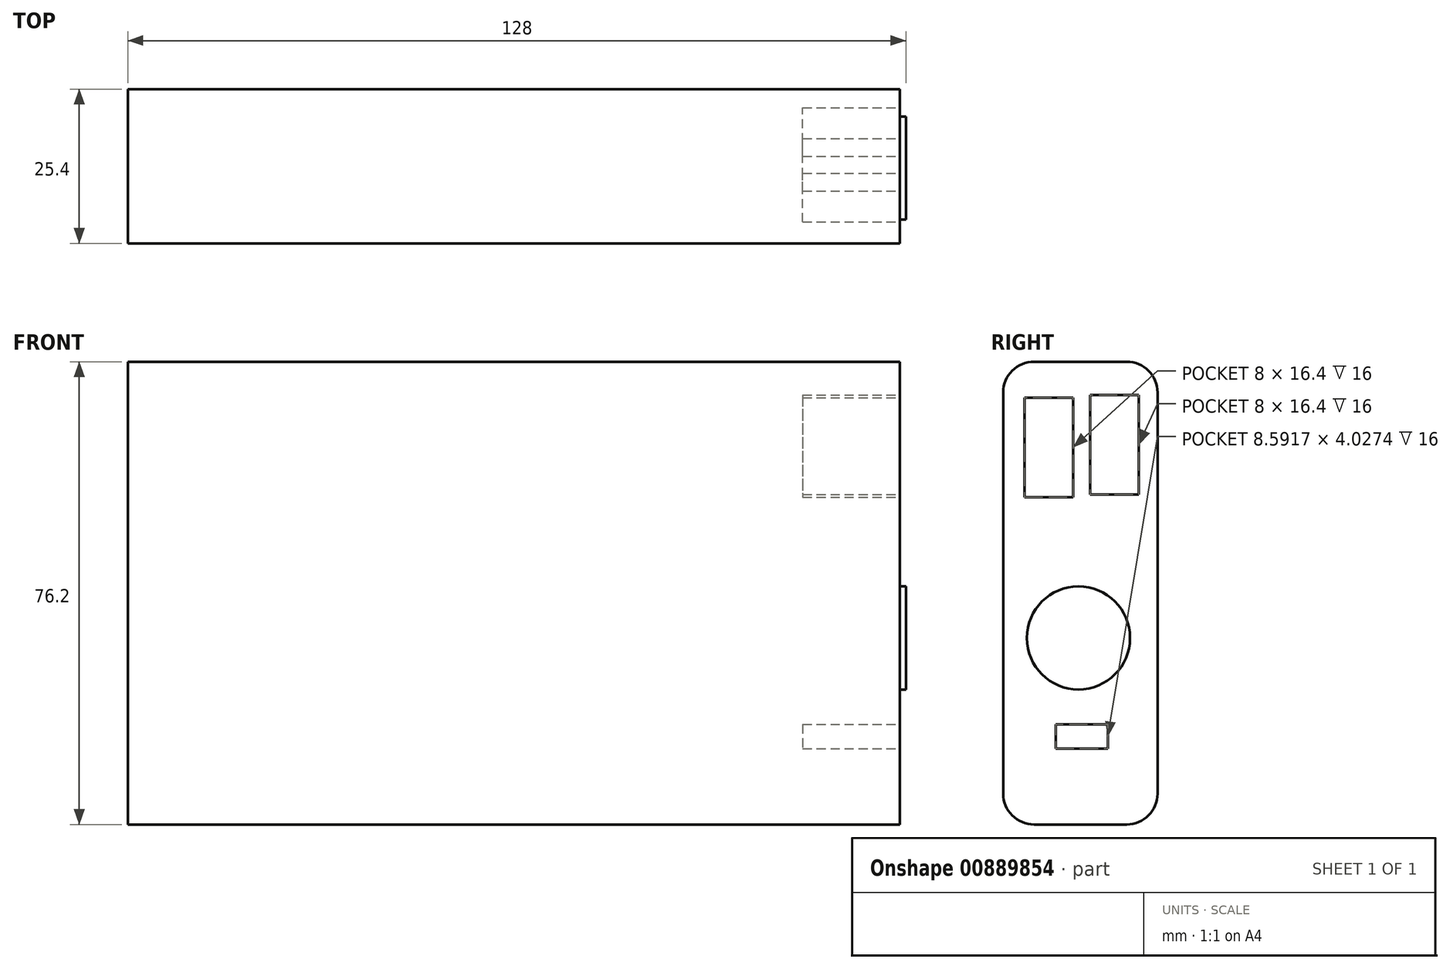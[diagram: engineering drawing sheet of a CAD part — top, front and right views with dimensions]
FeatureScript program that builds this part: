
annotation { "Feature Type Name" : "Feature", "Feature Type Description" : "" }
export const myFeature = defineFeature(function(context is Context, id is Id, definition is map)
    precondition{}
    {
        {
            var Q0;
            Q0=qCreatedBy(makeId("Front.planeOp"),FACE);
            var sketch = newSketch(context, id + "F0", { "sketchPlane" : qUnion([Q0])});
            skLineSegment(sketch, "E0.bottom", {"start": v(63.5, -38.1) * mm, "end": v(-63.5, -38.1) * mm});
            skLineSegment(sketch, "E0.top", {"start": v(63.5, 38.1) * mm, "end": v(-63.5, 38.1) * mm});
            skLineSegment(sketch, "E0.left", {"start": v(63.5, -38.1) * mm, "end": v(63.5, 38.1) * mm});
            skLineSegment(sketch, "E0.right", {"start": v(-63.5, -38.1) * mm, "end": v(-63.5, 38.1) * mm});
            skPoint(sketch, "E0.middle", {"position": v(0, 0) * mm});
            skSolve(sketch);
        }
        {
            var Q0;
            Q0 = qSketchRegion(id + "F0", true);
            extrude(context, id + "F1", {"entities" : qUnion([Q0]), "depth" : 25.4 * mm, "offsetDistance" : 25.4 * mm});
        }
        {
            var Q0;
            Q0=makeQuery(id+"F1.opExtrude","CAP_EDGE",EDGE,{"disambiguationData":[OSD([sQuery(id+"F0.wireOp",EDGE,"E0.top")])],"isStart":false});
            var Q1;
            Q1=makeQuery(id+"F1.opExtrude","CAP_EDGE",EDGE,{"disambiguationData":[OSD([sQuery(id+"F0.wireOp",EDGE,"E0.top")])],"isStart":true});
            var Q2;
            Q2=makeQuery(id+"F1.opExtrude","CAP_EDGE",EDGE,{"disambiguationData":[OSD([sQuery(id+"F0.wireOp",EDGE,"E0.bottom")])],"isStart":true});
            var Q3;
            Q3=makeQuery(id+"F1.opExtrude","CAP_EDGE",EDGE,{"disambiguationData":[OSD([sQuery(id+"F0.wireOp",EDGE,"E0.bottom")])],"isStart":false});
            fillet(context, id + "F2", {"entities" : qUnion([Q0, Q1, Q2, Q3]), "radius" : 5.08 * mm, "tangentPropagation" : true, "allowEdgeOverflow" : false});
        }
        {
            var Q0;
            Q0=makeQuery(id+"F1.opExtrude","SWEPT_FACE",FACE,{"disambiguationData":[OSD([sQuery(id+"F0.wireOp",EDGE,"E0.left")])]});
            var sketch = newSketch(context, id + "F3", { "sketchPlane" : qUnion([Q0])});
            skSolve(sketch);
        }
        {
            var Q0;
            {var subQ0=sQuery(id+"F0.wireOp",EDGE,"E0.left");Q0=makeQuery(id+"F3.imprint","IMPRINT",FACE,{"disambiguationData":[TD([[makeQuery(id+"F3.imprint","IMPRINT",EDGE,{"derivedFrom":makeQuery(id+"F1.opExtrude","CAP_EDGE",EDGE,{"disambiguationData":[OSD([subQ0])],"isStart":true})}),1.0]])]});}
            var sketch = newSketch(context, id + "F4", { "sketchPlane" : qUnion([Q0])});
            skLineSegment(sketch, "E1.bottom", {"start": v(-21.9, 32.19) * mm, "end": v(-13.9, 32.19) * mm});
            skLineSegment(sketch, "E1.top", {"start": v(-21.9, 15.79) * mm, "end": v(-13.9, 15.79) * mm});
            skLineSegment(sketch, "E1.left", {"start": v(-21.9, 32.19) * mm, "end": v(-21.9, 15.79) * mm});
            skLineSegment(sketch, "E1.right", {"start": v(-13.9, 32.19) * mm, "end": v(-13.9, 15.79) * mm});
            skSolve(sketch);
        }
        {
            var Q0;
            Q0=makeQuery(id+"F4.imprint","IMPRINT",FACE,{"disambiguationData":[TD([[makeQuery(id+"F4.imprint","IMPRINT",EDGE,{"derivedFrom":sQuery(id+"F4.wireOp",EDGE,"E1.bottom")}),-1.0]])]});
            extrude(context, id + "F5", {"entities" : qUnion([Q0]), "operationType" : NewBodyOperationType.REMOVE, "oppositeDirection" : true, "depth" : 16 * mm, "offsetDistance" : 25.4 * mm});
        }
        {
            var Q0;
            {var subQ0=sQuery(id+"F0.wireOp",EDGE,"E0.left");Q0=makeQuery(id+"F3.imprint","IMPRINT",FACE,{"disambiguationData":[TD([[makeQuery(id+"F3.imprint","IMPRINT",EDGE,{"derivedFrom":makeQuery(id+"F1.opExtrude","CAP_EDGE",EDGE,{"disambiguationData":[OSD([subQ0])],"isStart":true})}),1.0]])]});}
            var sketch = newSketch(context, id + "F6", { "sketchPlane" : qUnion([Q0])});
            skLineSegment(sketch, "E2.bottom", {"start": v(-11.07, 32.6) * mm, "end": v(-3.07, 32.6) * mm});
            skLineSegment(sketch, "E2.top", {"start": v(-11.07, 16.2) * mm, "end": v(-3.07, 16.2) * mm});
            skLineSegment(sketch, "E2.left", {"start": v(-11.07, 32.6) * mm, "end": v(-11.07, 16.2) * mm});
            skLineSegment(sketch, "E2.right", {"start": v(-3.07, 32.6) * mm, "end": v(-3.07, 16.2) * mm});
            skSolve(sketch);
        }
        {
            var Q0;
            Q0=makeQuery(id+"F6.imprint","IMPRINT",FACE,{"disambiguationData":[TD([[makeQuery(id+"F6.imprint","IMPRINT",EDGE,{"derivedFrom":sQuery(id+"F6.wireOp",EDGE,"E2.bottom")}),-1.0]])]});
            extrude(context, id + "F7", {"entities" : qUnion([Q0]), "operationType" : NewBodyOperationType.REMOVE, "oppositeDirection" : true, "depth" : 16 * mm, "offsetDistance" : 25.4 * mm});
        }
        {
            var Q0;
            {var subQ0=sQuery(id+"F0.wireOp",EDGE,"E0.left");Q0=makeQuery(id+"F3.imprint","IMPRINT",FACE,{"disambiguationData":[TD([[makeQuery(id+"F3.imprint","IMPRINT",EDGE,{"derivedFrom":makeQuery(id+"F1.opExtrude","CAP_EDGE",EDGE,{"disambiguationData":[OSD([subQ0])],"isStart":true})}),1.0]])]});}
            var sketch = newSketch(context, id + "F8", { "sketchPlane" : qUnion([Q0])});
            skCircle(sketch, "E3", {"center": v(-13.02, -7.38) * mm, "radius": 8.5 * mm});
            skSolve(sketch);
        }
        {
            var Q0;
            Q0=makeQuery(id+"F8.imprint","IMPRINT",FACE,{"disambiguationData":[TD([[makeQuery(id+"F8.imprint","IMPRINT",EDGE,{"derivedFrom":sQuery(id+"F8.wireOp",EDGE,"E3")}),1.0]])]});
            extrude(context, id + "F9", {"entities" : qUnion([Q0]), "operationType" : NewBodyOperationType.ADD, "depth" : 1 * mm, "offsetDistance" : 25.4 * mm});
        }
        {
            var Q0;
            {var subQ0=sQuery(id+"F0.wireOp",EDGE,"E0.left");Q0=makeQuery(id+"F3.imprint","IMPRINT",FACE,{"disambiguationData":[TD([[makeQuery(id+"F3.imprint","IMPRINT",EDGE,{"derivedFrom":makeQuery(id+"F1.opExtrude","CAP_EDGE",EDGE,{"disambiguationData":[OSD([subQ0])],"isStart":true})}),1.0]])]});}
            var sketch = newSketch(context, id + "F10", { "sketchPlane" : qUnion([Q0])});
            skLineSegment(sketch, "E4.bottom", {"start": v(-16.78, -21.61) * mm, "end": v(-8.19, -21.61) * mm});
            skLineSegment(sketch, "E4.top", {"start": v(-16.78, -25.64) * mm, "end": v(-8.19, -25.64) * mm});
            skLineSegment(sketch, "E4.left", {"start": v(-16.78, -21.61) * mm, "end": v(-16.78, -25.64) * mm});
            skLineSegment(sketch, "E4.right", {"start": v(-8.19, -21.61) * mm, "end": v(-8.19, -25.64) * mm});
            skSolve(sketch);
        }
        {
            var Q0;
            Q0=makeQuery(id+"F10.imprint","IMPRINT",FACE,{"disambiguationData":[TD([[makeQuery(id+"F10.imprint","IMPRINT",EDGE,{"derivedFrom":sQuery(id+"F10.wireOp",EDGE,"E4.bottom")}),-1.0]])]});
            extrude(context, id + "F11", {"entities" : qUnion([Q0]), "operationType" : NewBodyOperationType.REMOVE, "oppositeDirection" : true, "depth" : 16 * mm, "offsetDistance" : 25.4 * mm});
        }
    });
